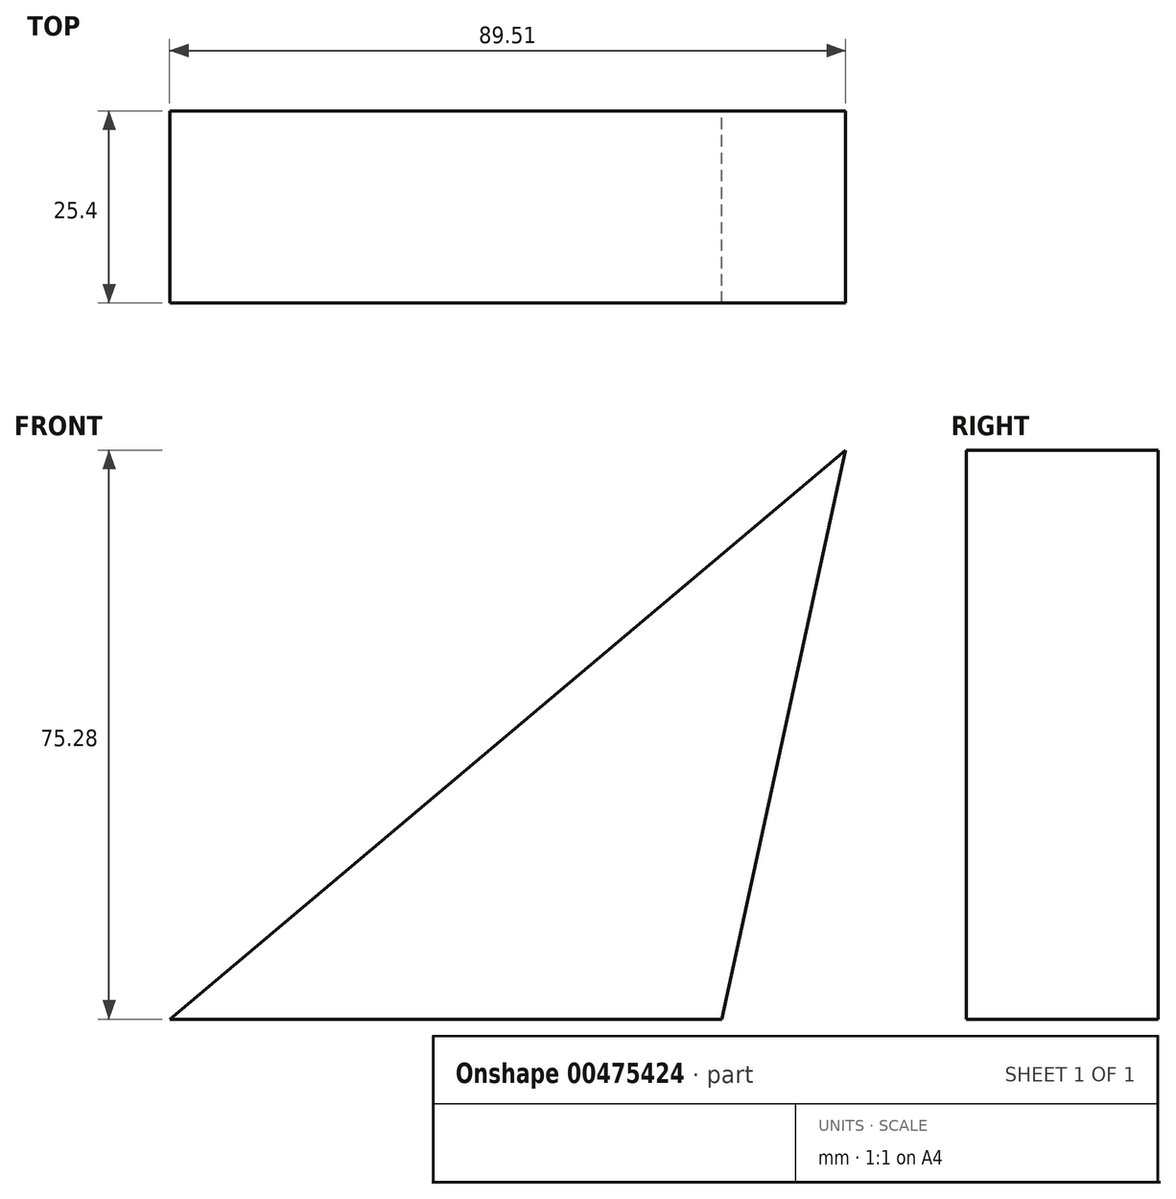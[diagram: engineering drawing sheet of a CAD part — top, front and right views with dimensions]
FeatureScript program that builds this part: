
annotation { "Feature Type Name" : "Feature", "Feature Type Description" : "" }
export const myFeature = defineFeature(function(context is Context, id is Id, definition is map)
    precondition{}
    {
        {
            var Q0;
            Q0=qCreatedBy(makeId("Front.planeOp"),FACE);
            var sketch = newSketch(context, id + "F0", { "sketchPlane" : qUnion([Q0])});
            skLineSegment(sketch, "E0", {"start": v(-73.14, 0) * mm, "end": v(0, 0) * mm});
            skLineSegment(sketch, "E1", {"start": v(-73.14, 0) * mm, "end": v(16.37, 75.28) * mm});
            skLineSegment(sketch, "E2", {"start": v(16.37, 75.28) * mm, "end": v(0, 0) * mm});
            skSolve(sketch);
        }
        {
            var Q0;
            Q0=qCreatedBy(makeId("Right.planeOp"),FACE);
            var sketch = newSketch(context, id + "F1", { "sketchPlane" : qUnion([Q0])});
            skSolve(sketch);
        }
        {
            var Q0;
            Q0=makeQuery(id+"F0.imprint","IMPRINT",FACE,{"disambiguationData":[TD([[makeQuery(id+"F0.imprint","IMPRINT",EDGE,{"derivedFrom":sQuery(id+"F0.wireOp",EDGE,"E0")}),1.0]])]});
            var Q1;
            Q1 = qSketchRegion(id + "F1", true);
            extrude(context, id + "F2", {"entities" : qUnion([Q0, Q1]), "depth" : 25.4 * mm});
        }
    });
